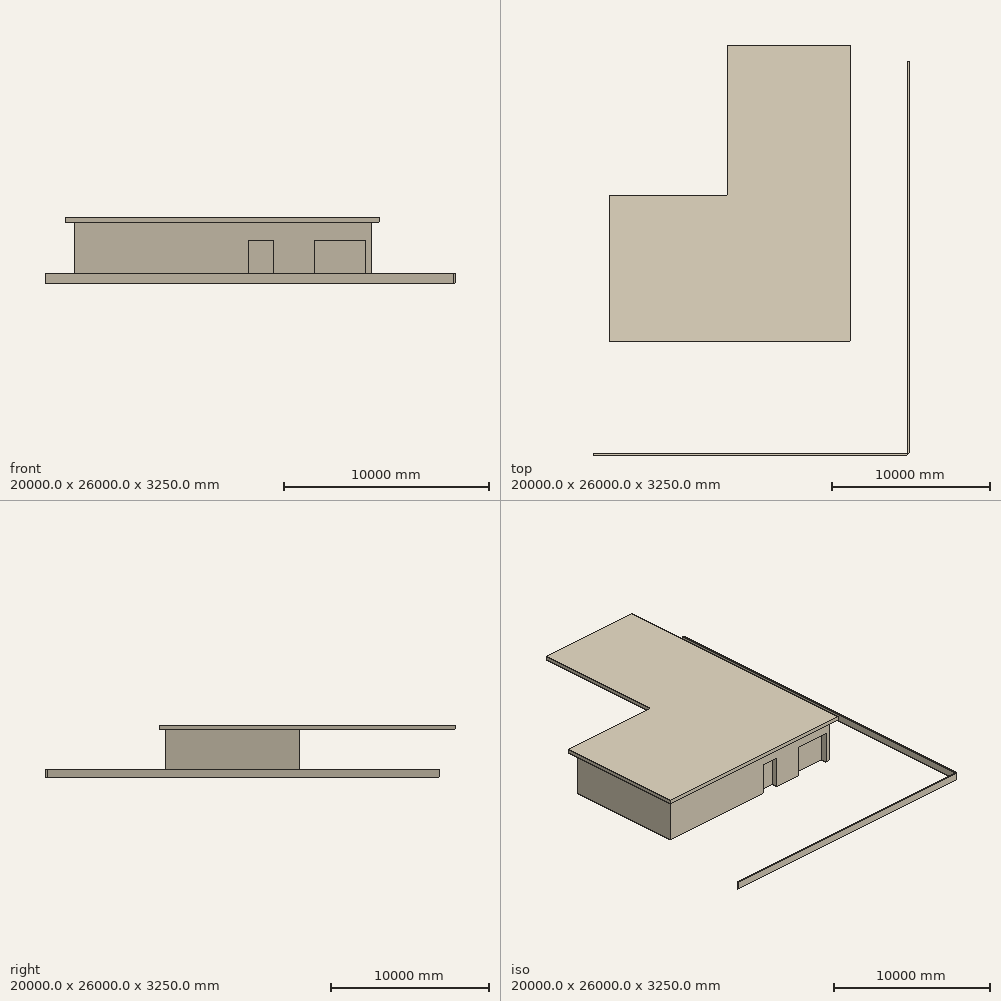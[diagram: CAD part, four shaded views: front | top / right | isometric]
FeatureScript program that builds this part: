
annotation { "Feature Type Name" : "Feature", "Feature Type Description" : "" }
export const myFeature = defineFeature(function(context is Context, id is Id, definition is map)
    precondition{}
    {
        {
            var Q0;
            Q0=qCreatedBy(makeId("Top.planeOp"),FACE);
            var sketch = newSketch(context, id + "F0", { "sketchPlane" : qUnion([Q0])});
            skLineSegment(sketch, "E0.bottom", {"start": v(7000, -8500) * mm, "end": v(-7500, -8500) * mm});
            skLineSegment(sketch, "E0.top", {"start": v(7000, 0) * mm, "end": v(-7500, 0) * mm});
            skLineSegment(sketch, "E0.left", {"start": v(7000, -8500) * mm, "end": v(7000, 0) * mm});
            skLineSegment(sketch, "E0.right", {"start": v(-7500, -8500) * mm, "end": v(-7500, 0) * mm});
            skLineSegment(sketch, "E1.bottom", {"start": v(7000, 0) * mm, "end": v(0, 0) * mm});
            skLineSegment(sketch, "E1.top", {"start": v(7000, 9500) * mm, "end": v(0, 9500) * mm});
            skLineSegment(sketch, "E1.left", {"start": v(7000, 0) * mm, "end": v(7000, 9500) * mm});
            skLineSegment(sketch, "E1.right", {"start": v(0, 0) * mm, "end": v(0, 9500) * mm});
            skSolve(sketch);
        }
        {
            var Q0;
            Q0=makeQuery(id+"F0.imprint","IMPRINT",FACE,{"disambiguationData":[TD([[makeQuery(id+"F0.imprint","IMPRINT",EDGE,{"derivedFrom":sQuery(id+"F0.wireOp",EDGE,"E1.bottom")}),-1.0]])]});
            var Q1;
            Q1=makeQuery(id+"F0.imprint","IMPRINT",FACE,{"disambiguationData":[TD([[makeQuery(id+"F0.imprint","IMPRINT",EDGE,{"derivedFrom":sQuery(id+"F0.wireOp",EDGE,"E0.bottom")}),-1.0]])]});
            extrude(context, id + "F5", {"entities" : qUnion([Q0, Q1]), "depth" : 3000 * mm});
        }
        {
            var Q0;
            Q0=makeQuery(id+"F5.opExtrude","SWEPT_FACE",FACE,{"disambiguationData":[OSD([sQuery(id+"F0.wireOp",EDGE,"E0.bottom")])]});
            var sketch = newSketch(context, id + "F1", { "sketchPlane" : qUnion([Q0])});
            skLineSegment(sketch, "E2.bottom", {"start": v(6700, 0) * mm, "end": v(4200, 0) * mm});
            skLineSegment(sketch, "E2.top", {"start": v(6700, 2100) * mm, "end": v(4200, 2100) * mm});
            skLineSegment(sketch, "E2.left", {"start": v(6700, 0) * mm, "end": v(6700, 2100) * mm});
            skLineSegment(sketch, "E2.right", {"start": v(4200, 0) * mm, "end": v(4200, 2100) * mm});
            skLineSegment(sketch, "E3.bottom", {"start": v(2199.77, 0) * mm, "end": v(999.77, 0) * mm});
            skLineSegment(sketch, "E3.top", {"start": v(2199.77, 2100) * mm, "end": v(999.77, 2100) * mm});
            skLineSegment(sketch, "E3.left", {"start": v(2199.77, 0) * mm, "end": v(2199.77, 2100) * mm});
            skLineSegment(sketch, "E3.right", {"start": v(999.77, 0) * mm, "end": v(999.77, 2100) * mm});
            skSolve(sketch);
        }
        {
            var Q0;
            Q0=makeQuery(id+"F1.imprint","IMPRINT",FACE,{"disambiguationData":[TD([[makeQuery(id+"F1.imprint","IMPRINT",EDGE,{"derivedFrom":sQuery(id+"F1.wireOp",EDGE,"E3.bottom")}),-1.0]])]});
            var Q1;
            Q1=makeQuery(id+"F1.imprint","IMPRINT",FACE,{"disambiguationData":[TD([[makeQuery(id+"F1.imprint","IMPRINT",EDGE,{"derivedFrom":sQuery(id+"F1.wireOp",EDGE,"E2.bottom")}),-1.0]])]});
            extrude(context, id + "F2", {"entities" : qUnion([Q0, Q1]), "operationType" : NewBodyOperationType.REMOVE, "oppositeDirection" : true, "depth" : 400 * mm});
        }
        {
            var Q0;
            Q0=qCreatedBy(makeId("Top.planeOp"),FACE);
            var sketch = newSketch(context, id + "F3", { "sketchPlane" : qUnion([Q0])});
            skLineSegment(sketch, "E4.bottom", {"start": v(11000, 8900) * mm, "end": v(11100, 8900) * mm});
            skLineSegment(sketch, "E4.top", {"start": v(11000, -16100) * mm, "end": v(11100, -16100) * mm});
            skLineSegment(sketch, "E4.left", {"start": v(11100, 8900) * mm, "end": v(11100, -16100) * mm});
            skLineSegment(sketch, "E4.right", {"start": v(11000, 8900) * mm, "end": v(11000, -16100) * mm});
            skLineSegment(sketch, "E5.bottom", {"start": v(11100, -16100) * mm, "end": v(-8900, -16100) * mm});
            skLineSegment(sketch, "E5.top", {"start": v(11100, -16000) * mm, "end": v(-8900, -16000) * mm});
            skLineSegment(sketch, "E5.left", {"start": v(11100, -16100) * mm, "end": v(11100, -16000) * mm});
            skLineSegment(sketch, "E5.right", {"start": v(-8900, -16100) * mm, "end": v(-8900, -16000) * mm});
            skSolve(sketch);
        }
        {
            var Q0;
            {var subQ0=sQuery(id+"F3.wireOp",EDGE,"E4.bottom");Q0=makeQuery(id+"F3.imprint","IMPRINT",FACE,{"disambiguationData":[TD([[makeQuery(id+"F3.imprint","IMPRINT",EDGE,{"derivedFrom":subQ0}),-1.0]])]});}
            var Q1;
            {var subQ5=sQuery(id+"F3.wireOp",EDGE,"E5.right");Q1=makeQuery(id+"F3.imprint","IMPRINT",FACE,{"disambiguationData":[TD([[makeQuery(id+"F3.imprint","IMPRINT",EDGE,{"derivedFrom":subQ5}),-1.0]])]});}
            var Q2;
            {var subQ5=sQuery(id+"F3.wireOp",EDGE,"E5.left");Q2=makeQuery(id+"F3.imprint","IMPRINT",FACE,{"disambiguationData":[TD([[makeQuery(id+"F3.imprint","IMPRINT",EDGE,{"derivedFrom":subQ5}),1.0]])]});}
            extrude(context, id + "F4", {"entities" : qUnion([Q0, Q1, Q2]), "depth" : 500 * mm});
        }
        {
            var Q0;
            Q0=makeQuery(id+"F5.opExtrude","CAP_FACE",FACE,{"disambiguationData":[OSD([sQuery(id+"F0.wireOp",EDGE,"E0.bottom"),sQuery(id+"F0.wireOp",EDGE,"E0.top"),sQuery(id+"F0.wireOp",EDGE,"E0.left"),sQuery(id+"F0.wireOp",EDGE,"E0.right"),sQuery(id+"F0.wireOp",EDGE,"E1.top"),sQuery(id+"F0.wireOp",EDGE,"E1.left"),sQuery(id+"F0.wireOp",EDGE,"E1.right")])],"isStart":false});
            var sketch = newSketch(context, id + "F6", { "sketchPlane" : qUnion([Q0])});
            skLineSegment(sketch, "E6", {"start": v(-7900, -8900) * mm, "end": v(7400, -8900) * mm});
            skLineSegment(sketch, "E7", {"start": v(-7900, -8900) * mm, "end": v(-7900, 400) * mm});
            skLineSegment(sketch, "E8", {"start": v(-7900, 400) * mm, "end": v(-400, 400) * mm});
            skLineSegment(sketch, "E9", {"start": v(-400, 400) * mm, "end": v(-400, 9900) * mm});
            skLineSegment(sketch, "E10", {"start": v(-400, 9900) * mm, "end": v(7400, 9900) * mm});
            skLineSegment(sketch, "E11", {"start": v(7400, 9900) * mm, "end": v(7400, -8900) * mm});
            skSolve(sketch);
        }
        {
            var Q0;
            Q0=makeQuery(id+"F6.imprint","IMPRINT",FACE,{"disambiguationData":[TD([[makeQuery(id+"F6.imprint","IMPRINT",EDGE,{"derivedFrom":makeQuery(id+"F5.opExtrude","CAP_EDGE",EDGE,{"disambiguationData":[OSD([sQuery(id+"F0.wireOp",EDGE,"E0.bottom")])],"isStart":false})}),-1.0]])]});
            var Q1;
            Q1=makeQuery(id+"F6.imprint","IMPRINT",FACE,{"disambiguationData":[TD([[makeQuery(id+"F6.imprint","IMPRINT",EDGE,{"derivedFrom":sQuery(id+"F6.wireOp",EDGE,"E6")}),1.0]])]});
            extrude(context, id + "F7", {"entities" : qUnion([Q0, Q1]), "operationType" : NewBodyOperationType.ADD, "depth" : 250 * mm});
        }
    });
